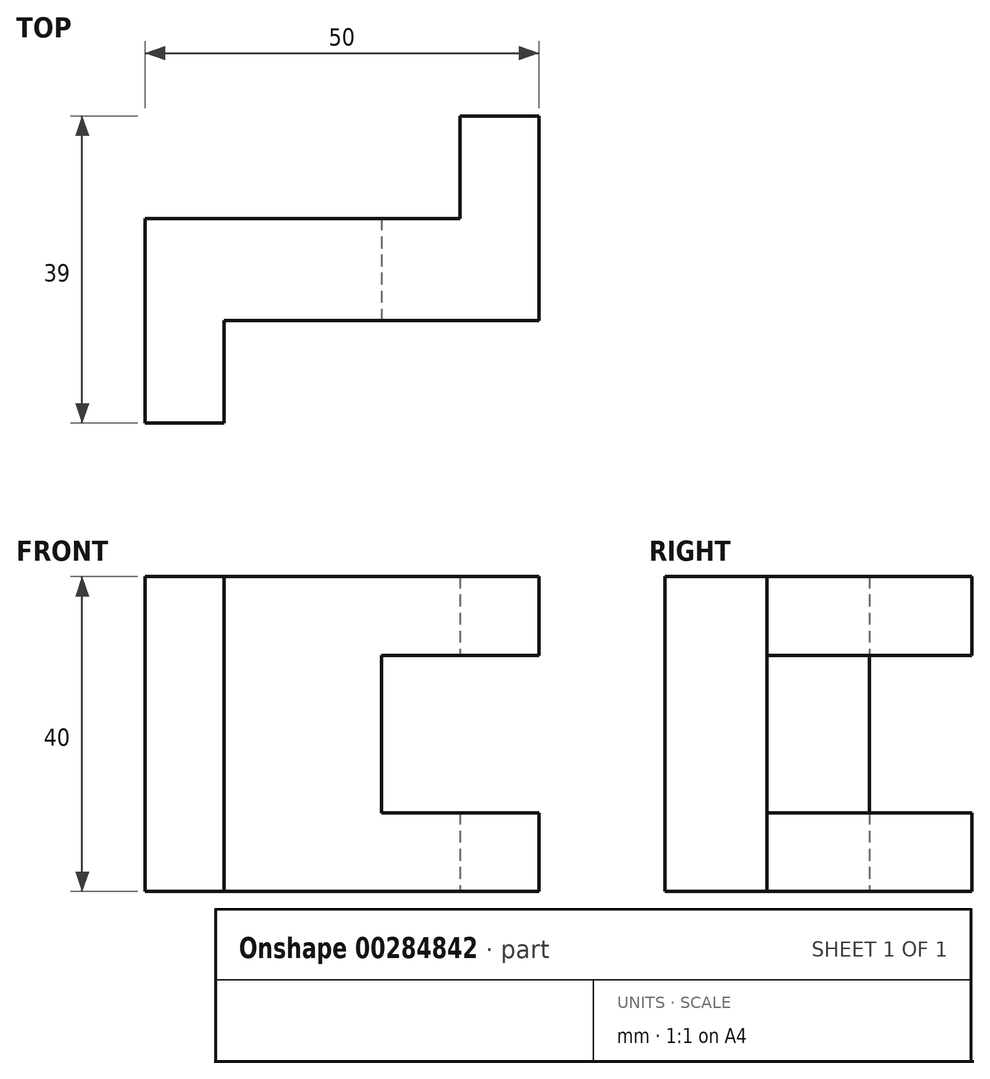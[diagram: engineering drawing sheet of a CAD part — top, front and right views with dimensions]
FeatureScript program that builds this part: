
annotation { "Feature Type Name" : "Feature", "Feature Type Description" : "" }
export const myFeature = defineFeature(function(context is Context, id is Id, definition is map)
    precondition{}
    {
        {
            var Q0;
            Q0=qCreatedBy(makeId("Top.planeOp"),FACE);
            var sketch = newSketch(context, id + "F0", { "sketchPlane" : qUnion([Q0])});
            skLineSegment(sketch, "E0.bottom", {"start": v(0, 0) * mm, "end": v(50, 0) * mm});
            skLineSegment(sketch, "E0.top", {"start": v(0, 39) * mm, "end": v(50, 39) * mm});
            skLineSegment(sketch, "E0.left", {"start": v(0, 0) * mm, "end": v(0, 39) * mm});
            skLineSegment(sketch, "E0.right", {"start": v(50, 0) * mm, "end": v(50, 39) * mm});
            skLineSegment(sketch, "E1", {"start": v(10, 0) * mm, "end": v(10, 13) * mm});
            skLineSegment(sketch, "E2", {"start": v(10, 13) * mm, "end": v(50, 13) * mm});
            skLineSegment(sketch, "E3", {"start": v(40, 39) * mm, "end": v(40, 26) * mm});
            skLineSegment(sketch, "E4", {"start": v(40, 26) * mm, "end": v(0, 26) * mm});
            skSolve(sketch);
        }
        {
            var Q0;
            {var subQ9=sQuery(id+"F0.wireOp",EDGE,"E1");Q0=makeQuery(id+"F0.imprint","IMPRINT",FACE,{"disambiguationData":[TD([[makeQuery(id+"F0.imprint","IMPRINT",EDGE,{"derivedFrom":subQ9}),1.0]])]});}
            extrude(context, id + "F1", {"entities" : qUnion([Q0]), "depth" : 40 * mm, "symmetric" : true});
        }
        {
            var Q0;
            Q0=makeQuery(id+"F1.opExtrude","SWEPT_FACE",FACE,{"disambiguationData":[OSD([sQuery(id+"F0.wireOp",EDGE,"E2")])]});
            var sketch = newSketch(context, id + "F2", { "sketchPlane" : qUnion([Q0])});
            skLineSegment(sketch, "E5.bottom", {"start": v(50, 10) * mm, "end": v(30, 10) * mm});
            skLineSegment(sketch, "E5.top", {"start": v(50, -10) * mm, "end": v(30, -10) * mm});
            skLineSegment(sketch, "E5.left", {"start": v(50, 10) * mm, "end": v(50, -10) * mm});
            skLineSegment(sketch, "E5.right", {"start": v(30, 10) * mm, "end": v(30, -10) * mm});
            skSolve(sketch);
        }
        {
            var Q0;
            Q0=qSketchRegion(id+"F2",true);
            extrude(context, id + "F3", {"entities" : qUnion([Q0]), "operationType" : NewBodyOperationType.REMOVE, "endBound" : BoundingType.THROUGH_ALL, "oppositeDirection" : true, "depth" : 25 * mm});
        }
    });
